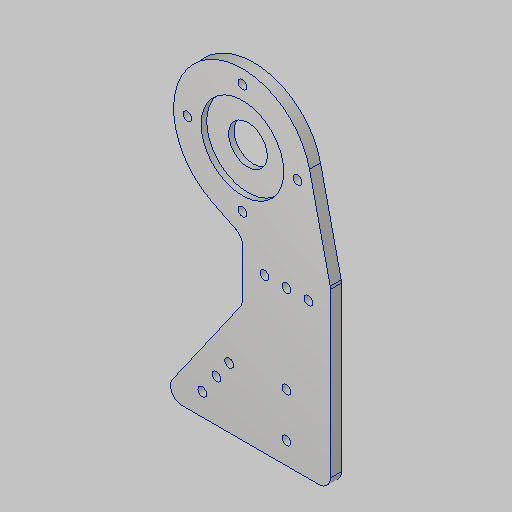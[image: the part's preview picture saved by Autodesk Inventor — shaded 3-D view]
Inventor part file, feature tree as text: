
AUTODESK INVENTOR PART (.ipt)
format: ipt  version: 2023.5 (Build 275446000, 446)  size: 152,064 bytes
history: native  units: in
note: dims shown in document units (in); Inventor stores cm internally (conversion verified against a paired STEP export)
features: other x3, sketch x3
ambient origin geometry x8: Origin, YZ Plane, XZ Plane, XY Plane, X Axis, Y Axis, Z Axis, Center Point
bodies: Solid1 (feature_tree)
feature tree (6):
  other  "CL7-010.ipt"
  other  "Solid1::CL7-010.ipt"
  other  "TaggingFeature1"
  sketch  "Sketch1"  dims[d0=0.3937in]
  sketch  "Sketch2"
  sketch  "Sketch3"
